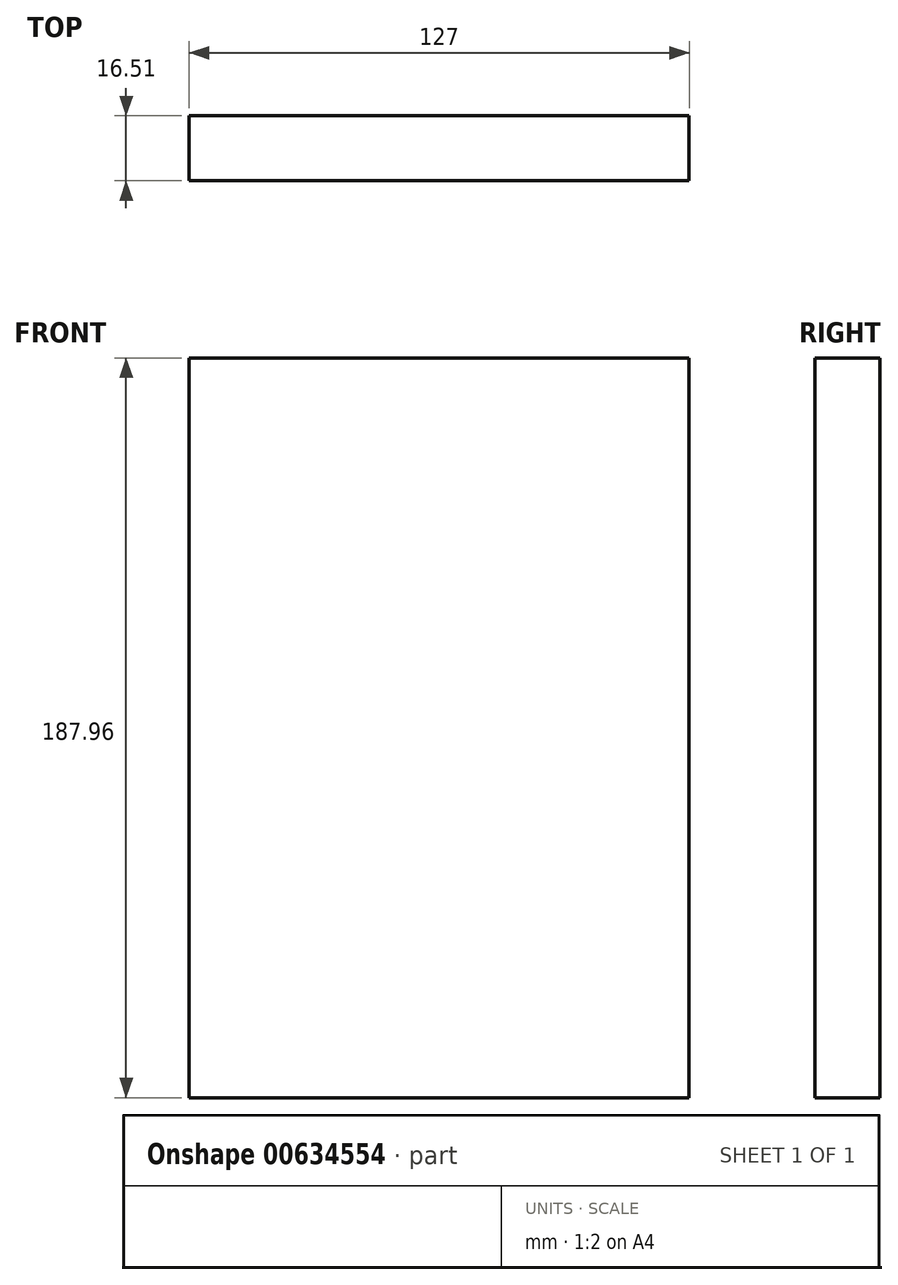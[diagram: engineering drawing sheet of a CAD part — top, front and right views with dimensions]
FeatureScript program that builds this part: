
annotation { "Feature Type Name" : "Feature", "Feature Type Description" : "" }
export const myFeature = defineFeature(function(context is Context, id is Id, definition is map)
    precondition{}
    {
        {
            var Q0;
            Q0=qCreatedBy(makeId("Front.planeOp"),FACE);
            var sketch = newSketch(context, id + "F0", { "sketchPlane" : qUnion([Q0])});
            skLineSegment(sketch, "E0.bottom", {"start": v(-56.51, 97.34) * mm, "end": v(70.49, 97.34) * mm});
            skLineSegment(sketch, "E0.top", {"start": v(-56.51, -90.62) * mm, "end": v(70.49, -90.62) * mm});
            skLineSegment(sketch, "E0.left", {"start": v(-56.51, 97.34) * mm, "end": v(-56.51, -90.62) * mm});
            skLineSegment(sketch, "E0.right", {"start": v(70.49, 97.34) * mm, "end": v(70.49, -90.62) * mm});
            skSolve(sketch);
        }
        {
            var Q0;
            Q0 = qSketchRegion(id + "F0", true);
            extrude(context, id + "F1", {"entities" : qUnion([Q0]), "depth" : 16.5 * mm, "offsetDistance" : 25.4 * mm});
        }
    });
